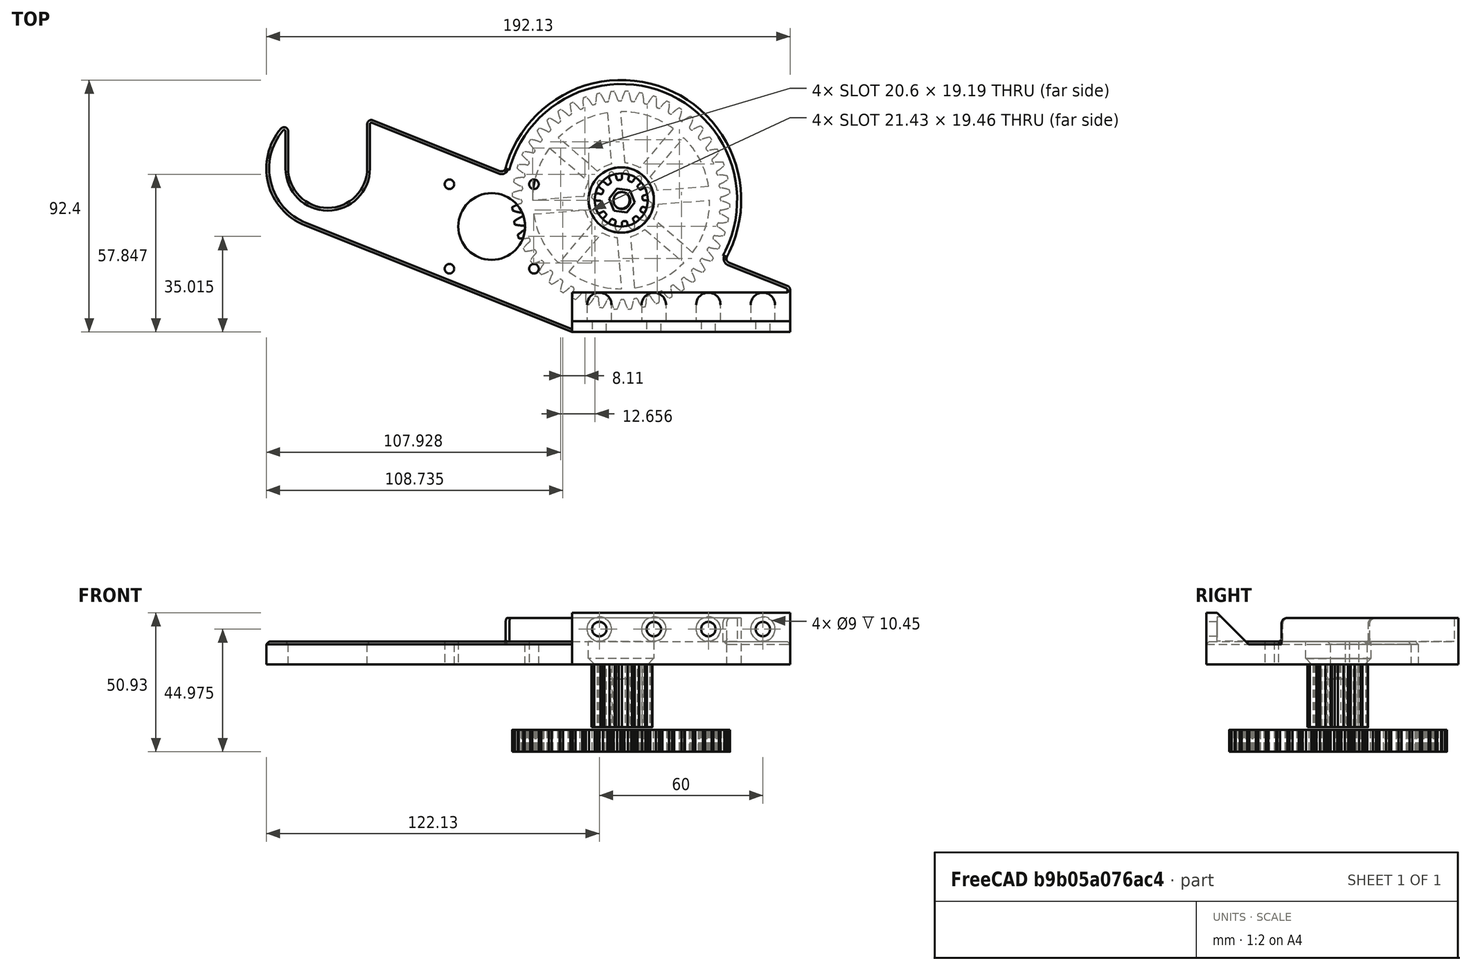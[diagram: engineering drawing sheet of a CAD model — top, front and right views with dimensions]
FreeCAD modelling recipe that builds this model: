
FCSTD DOCUMENT  (FreeCAD 0.20R29177 (Git))
Label: Spool Holder_-_Part_5B_-_48t straight
License: All rights reserved
LicenseURL: http://en.wikipedia.org/wiki/All_rights_reserved
objects: Sketcher::SketchObject×7, PartDesign::Pad×3, PartDesign::Pocket×3, PartDesign::Chamfer×3, Part::Feature×2, Mesh::Feature×2, PartDesign::Plane×2, App::Part×1, PartDesign::Fillet×1, PartDesign::Body×1
note: 32 computed .brp shape members not serialized (recipe doc carries the construction recipe); baked Part::Feature solids carry a one-line shape summary decoded from their .brp

FEATURE [Sketcher::SketchObject] Sketch002
  FullyConstrained = false
  MapMode = 5
  sketch-geometry (26):
    g0: ArcOfCircle CenterX=-129.63 CenterY=60 CenterZ=0 NormalX=0 NormalY=0 NormalZ=1 AngleXU=0 Radius=14.5 StartAngle=3.14159 EndAngle=6.28317
    g1: ArcOfCircle CenterX=-129.63 CenterY=60 CenterZ=0 NormalX=0 NormalY=0 NormalZ=1 AngleXU=0 Radius=22.5 StartAngle=2.43705 EndAngle=4.33263
    g2: LineSegment StartX=-40 StartY=0 StartZ=0 EndX=40 EndY=0 EndZ=0
    g3: LineSegment StartX=40 StartY=0 StartZ=0 EndX=40 EndY=15.5052 EndZ=0
    g4: LineSegment StartX=-40 StartY=0 StartZ=0 EndX=-137.971 EndY=39.103 EndZ=0
    g5: LineSegment StartX=-113.074 StartY=77.618 StartZ=0 EndX=-66.4027 EndY=58.9901 EndZ=0
    g6: Circle CenterX=-69.469 CenterY=38.6797 CenterZ=0 NormalX=0 NormalY=0 NormalZ=1 AngleXU=0 Radius=12.25
    g7: Circle CenterX=-21.953 CenterY=48.4 CenterZ=0 NormalX=0 NormalY=0 NormalZ=1 AngleXU=0 Radius=9.75
    g8: LineSegment StartX=-144.13 StartY=60 StartZ=0 EndX=-144.13 EndY=73.6015 EndZ=0
    g9: LineSegment StartX=-115.13 StartY=59.9997 StartZ=0 EndX=-115.13 EndY=76.2248 EndZ=0
    g10: ArcOfCircle CenterX=-145.63 CenterY=73.6015 CenterZ=0 NormalX=0 NormalY=0 NormalZ=1 AngleXU=0 Radius=1.5 StartAngle=3e-15 EndAngle=2.43705
    g11: ArcOfCircle CenterX=-113.63 CenterY=76.2248 CenterZ=0 NormalX=0 NormalY=0 NormalZ=1 AngleXU=0 Radius=1.5 StartAngle=1.19104 EndAngle=3.14159
    g12: ArcOfCircle CenterX=38.5 CenterY=15.5052 CenterZ=0 NormalX=0 NormalY=0 NormalZ=1 AngleXU=0 Radius=1.5 StartAngle=0 EndAngle=1.19104
    g13: ArcOfCircle CenterX=-21.953 CenterY=48.4 CenterZ=0 NormalX=0 NormalY=0 NormalZ=1 AngleXU=0 Radius=44 StartAngle=5.79018 EndAngle=9.15827
    g14: LineSegment StartX=17.5726 StartY=25.473 StartZ=0 EndX=39.056 EndY=16.8983 EndZ=0
    g15: ArcOfCircle CenterX=18.1287 CenterY=26.8661 CenterZ=0 NormalX=0 NormalY=0 NormalZ=1 AngleXU=0 Radius=1.5 StartAngle=2.64859 EndAngle=4.33263
    g16: ArcOfCircle CenterX=-65.8467 CenterY=60.3832 CenterZ=0 NormalX=0 NormalY=0 NormalZ=1 AngleXU=0 Radius=1.5 StartAngle=4.33263 EndAngle=6.01667
    g17: LineSegment StartX=-53.969 StartY=23.1797 StartZ=0 EndX=-53.969 EndY=54.1797 EndZ=0
    g18: LineSegment StartX=-53.969 StartY=54.1797 StartZ=0 EndX=-84.969 EndY=54.1797 EndZ=0
    g19: LineSegment StartX=-84.969 StartY=54.1797 StartZ=0 EndX=-84.969 EndY=23.1797 EndZ=0
    g20: LineSegment StartX=-84.969 StartY=23.1797 StartZ=0 EndX=-53.969 EndY=23.1797 EndZ=0
    g21: GeomPoint X=-69.469 Y=38.6797 Z=0
    g22: Circle CenterX=-84.969 CenterY=23.1797 CenterZ=0 NormalX=0 NormalY=0 NormalZ=1 AngleXU=0 Radius=1.75
    g23: Circle CenterX=-84.969 CenterY=54.1797 CenterZ=0 NormalX=0 NormalY=0 NormalZ=1 AngleXU=0 Radius=1.75
    g24: Circle CenterX=-53.969 CenterY=54.1797 CenterZ=0 NormalX=0 NormalY=0 NormalZ=1 AngleXU=0 Radius=1.75
    g25: Circle CenterX=-53.969 CenterY=23.1797 CenterZ=0 NormalX=0 NormalY=0 NormalZ=1 AngleXU=0 Radius=1.75
  constraints (64):
    c: Diameter(g0) = 29
    c: Coincident(g1,g0)
    c: Diameter(g1) = 45
    c: PointOnObject(g2,g-1)
    c: PointOnObject(g2,g-1)
    c: Vertical(g3)
    c: DistanceX(g0) = -129.63
    c: DistanceY(g-1,g0) = 60
    c: Parallel(g5,g4)
    c: Diameter(g6) = 24.5
    c: Diameter(g7) = 19.5
    c: Distance(g7,g0) = 108.3
    c: Distance(g6,g7) = 48.5
    c: DistanceY(g4,g7) = 48.4
    c: Vertical(g8)
    c: Tangent(g0,g8) = 1.5708
    c: Vertical(g9)
    c: Tangent(g1,g4) = 1.5708
    c: Tangent(g8,g10) = -1.5708
    c: Tangent(g1,g10) = -1.5708
    c: Diameter(g10) = 3
    c: Tangent(g5,g11) = 1.5708
    c: Tangent(g9,g11) = 1.5708
    c: Diameter(g11) = 3
    c: Tangent(g3,g12) = -1.5708
    c: Diameter(g12) = 3
    c: DistanceX(g2,g-1) = 40
    c: DistanceX(g2,g2) = 80
    c: Coincident(g4,g2)
    c: Distance(g6,g4) = 25
    c: Coincident(g9,g0)
    c: Distance(g2,g5) = 45
    c: Coincident(g3,g2)
    c: Tangent(g13,g15) = 1.5708
    c: Tangent(g14,g15) = -1.5708
    c: Tangent(g13,g16) = 1.5708
    c: Tangent(g5,g16) = -1.5708
    c: Equal(g12,g15)
    c: Equal(g15,g16)
    c: Diameter(g13) = 88
    c: Coincident(g7,g13)
    c: PointOnObject(g14,g5)
    c: PointOnObject(g12,g5)
    c: Tangent(g14,g12) = 1.5708
    c: Coincident(g17,g18)
    c: Coincident(g18,g19)
    c: Coincident(g19,g20)
    c: Coincident(g20,g17)
    c: Horizontal(g18)
    c: Horizontal(g20)
    c: Vertical(g17)
    c: Vertical(g19)
    c: Symmetric(g18,g17,g21)
    c: Coincident(g21,g6)
    c: DistanceX(g18,g18) = 31
    c: Equal(g18,g19)
    c: Coincident(g22,g19)
    c: Coincident(g23,g18)
    c: Coincident(g24,g17)
    c: Coincident(g25,g17)
    c: Equal(g22,g23)
    c: Equal(g23,g24)
    c: Equal(g24,g25)
    c: Diameter(g22) = 3.5
FEATURE [PartDesign::Pad] Pad
  Direction = (0,0,1)
  Length = 8.425
  Length2 = 10
  Profile = -> Sketch002
  ReferenceAxis = -> Sketch002 [N_Axis]
  Type = 0
FEATURE [Part::Feature] Part__Feature  label="PolarPattern"
  Placement = pos=(-22,48.3,-9) rot=(0,0,1;1.64934rad)
  shape: bbox 79.95 x 79.95 x 8 mm, 323 faces (baked)
FEATURE [Part::Feature] Part__Feature001  label="Cut002"
  Placement = pos=(-21.7,48.2,0) rot=(0,0,-1;0.143117rad)
  shape: bbox 22.29 x 22.29 x 23 mm, 106 faces (baked)
FEATURE [App::Part] TOP___Part_5C___DoubleGear48t
  Group = -> [Part__Feature,Part__Feature001]
  Origin = -> Origin001
  Placement = pos=(0,0,38) rot=(0,0,1;0rad)
FEATURE [Sketcher::SketchObject] Sketch
  ExternalGeometry = -> [Pad]
  FullyConstrained = false
  MapMode = 5
  Support = -> [XY_Plane]
  sketch-geometry (4):
    g0: ArcOfCircle CenterX=-21.9529 CenterY=48.4002 CenterZ=0 NormalX=0 NormalY=0 NormalZ=1 AngleXU=0 Radius=42.51 StartAngle=5.78619 EndAngle=9.16226
    g1: LineSegment StartX=-64.3996 StartY=59.9882 StartZ=0 EndX=-63.0065 EndY=59.4321 EndZ=0
    g2: LineSegment StartX=15.4142 StartY=28.1321 StartZ=0 EndX=16.8073 EndY=27.576 EndZ=0
    g3: ArcOfCircle CenterX=-21.9529 CenterY=48.4002 CenterZ=0 NormalX=0 NormalY=0 NormalZ=1 AngleXU=0 Radius=44 StartAngle=5.79018 EndAngle=9.15827
  constraints (10):
    c: Coincident(g1,g-3)
    c: Coincident(g2,g-3)
    c: Coincident(g0,g1)
    c: Coincident(g0,g2)
    c: Equal(g1,g2)
    c: Distance(g1) = 1.5
    c: Parallel(g1,g2)
    c: Coincident(g3,g0)
    c: Coincident(g3,g2)
    c: Coincident(g3,g1)
FEATURE [PartDesign::Pad] Pad001
  BaseFeature = -> Pad
  Direction = (0,0,1)
  Length = 17
  Length2 = 10
  Profile = -> Sketch
  ReferenceAxis = -> Sketch [N_Axis]
  Type = 0
FEATURE [Mesh::Feature] RECREATOR3D___Part_6A___Spool_Gear  label="RECREATOR3D - Part 6A - Spool Gear"
  Placement = pos=(-129.6,60,0) rot=(0,0,1;0.07854rad)
FEATURE [Mesh::Feature] RECREATOR3D___Part_8___Small_Gear_WIDER  label="RECREATOR3D - Part 8 - Small Gear WIDER"
  Placement = pos=(-69.3,38.6,0) rot=(0,0,1;0.106465rad)
FEATURE [Sketcher::SketchObject] Sketch003
  ExternalGeometry = -> [Pad001]
  FullyConstrained = true
  MapMode = 5
  Placement = pos=(0,0,0) rot=(0.57735,0.57735,0.57735;2.0944rad)
  Support = -> [YZ_Plane]
  sketch-geometry (4):
    g0: LineSegment StartX=0 StartY=18.925 StartZ=0 EndX=4 EndY=18.925 EndZ=0
    g1: LineSegment StartX=4 StartY=18.925 StartZ=0 EndX=14.5 EndY=8.425 EndZ=0
    g2: LineSegment StartX=0 StartY=8.425 StartZ=0 EndX=14.5 EndY=8.425 EndZ=0
    g3: LineSegment StartX=0 StartY=18.925 StartZ=0 EndX=0 EndY=8.425 EndZ=0
  constraints (11):
    c: PointOnObject(g0,g-2)
    c: Horizontal(g0)
    c: Coincident(g1,g0)
    c: PointOnObject(g1,g-3)
    c: Angle(g0,g1) = 2.35619
    c: DistanceX(g0,g0) = 4
    c: Coincident(g2,g-3)
    c: Coincident(g2,g1)
    c: Coincident(g3,g0)
    c: DistanceY(g3,g3) = 10.5
    c: Coincident(g3,g2)
FEATURE [PartDesign::Pad] Pad002
  BaseFeature = -> Pad001
  Direction = (1,-2e-16,3e-16)
  Length = 40
  Length2 = 40
  Profile = -> Sketch003
  ReferenceAxis = -> Sketch003 [N_Axis]
  Type = 4
FEATURE [Sketcher::SketchObject] Sketch004
  ExternalGeometry = -> [Pad002]
  FullyConstrained = false
  MapMode = 5
  Placement = pos=(0,0,0) rot=(1,0,0;1.5708rad)
  Support = -> [XZ_Plane]
  sketch-geometry (7):
    g0: Circle CenterX=30 CenterY=12.975 CenterZ=0 NormalX=0 NormalY=0 NormalZ=1 AngleXU=0 Radius=2.65
    g1: Circle CenterX=10 CenterY=12.975 CenterZ=0 NormalX=0 NormalY=0 NormalZ=1 AngleXU=0 Radius=2.65
    g2: LineSegment StartX=30 StartY=12.975 StartZ=0 EndX=10 EndY=12.975 EndZ=0
    g3: Circle CenterX=-10 CenterY=12.975 CenterZ=0 NormalX=0 NormalY=0 NormalZ=1 AngleXU=0 Radius=2.65
    g4: LineSegment StartX=10 StartY=12.975 StartZ=0 EndX=-10 EndY=12.975 EndZ=0
    g5: Circle CenterX=-30 CenterY=12.975 CenterZ=0 NormalX=0 NormalY=0 NormalZ=1 AngleXU=0 Radius=2.65
    g6: LineSegment StartX=-10 StartY=12.975 StartZ=0 EndX=-30 EndY=12.975 EndZ=0
  constraints (16):
    c: Diameter(g0) = 5.3
    c: Diameter(g1) = 5.3
    c: Coincident(g0,g2)
    c: Coincident(g1,g2)
    c: Distance(g2) = 20
    c: Angle(g2) = 3.14159
    c: Diameter(g3) = 5.3
    c: Coincident(g1,g4)
    c: Coincident(g3,g4)
    c: Equal(g2,g4)
    c: Parallel(g4,g2)
    c: Diameter(g5) = 5.3
    c: Coincident(g3,g6)
    c: Coincident(g5,g6)
    c: Equal(g2,g6)
    c: Parallel(g6,g2)
FEATURE [PartDesign::Pocket] Pocket
  BaseFeature = -> Pad002
  Direction = (0,1,2e-16)
  Length = 18
  Length2 = 5
  Profile = -> Sketch004
  ReferenceAxis = -> Sketch004 [N_Axis]
  Type = 0
FEATURE [PartDesign::Plane] DatumPlane  label="CounterBorePlane"
  AttachmentOffset = pos=(0,0,-4) rot=(0,0,1;0rad)
  Length = 211.732
  MapMode = 5
  Placement = pos=(9e-16,4,-9e-16) rot=(1,0,0;1.5708rad)
  ResizeMode = 0
  Support = -> [Pocket]
  Width = 69.6025
FEATURE [Sketcher::SketchObject] Sketch005
  ExternalGeometry = -> [Pocket]
  FullyConstrained = false
  MapMode = 5
  Placement = pos=(9e-16,4,-9e-16) rot=(1,0,0;1.5708rad)
  Support = -> [DatumPlane]
  sketch-geometry (4):
    g0: Circle CenterX=-30 CenterY=12.975 CenterZ=0 NormalX=0 NormalY=0 NormalZ=1 AngleXU=0 Radius=4.5
    g1: Circle CenterX=-10 CenterY=12.975 CenterZ=0 NormalX=0 NormalY=0 NormalZ=1 AngleXU=0 Radius=4.5
    g2: Circle CenterX=10 CenterY=12.975 CenterZ=0 NormalX=0 NormalY=0 NormalZ=1 AngleXU=0 Radius=4.5
    g3: Circle CenterX=30 CenterY=12.975 CenterZ=0 NormalX=0 NormalY=0 NormalZ=1 AngleXU=0 Radius=4.5
  constraints (7):
    c: Coincident(g1,g-4)
    c: Coincident(g2,g-5)
    c: Coincident(g3,g-6)
    c: Diameter(g3) = 9
    c: Equal(g3,g2)
    c: Equal(g2,g1)
    c: Equal(g1,g0)
FEATURE [PartDesign::Pocket] Pocket001
  BaseFeature = -> Pocket
  Direction = (2e-16,1,-2e-16)
  Length = 12
  Length2 = 5
  Profile = -> Sketch005
  ReferenceAxis = -> Sketch005 [N_Axis]
  Type = 0
FEATURE [Sketcher::SketchObject] Sketch006
  FullyConstrained = true
  MapMode = 5
  Support = -> [XY_Plane]
FEATURE [PartDesign::Plane] DatumPlane001
  Length = 222.164
  MapMode = 5
  Placement = pos=(0,0,8.425) rot=(0,0,1;0rad)
  ResizeMode = 0
  Support = -> [Pad001]
  Width = 147.415
FEATURE [Sketcher::SketchObject] Sketch007
  ExternalGeometry = -> [Pad001]
  FullyConstrained = true
  MapMode = 5
  Placement = pos=(0,0,8.425) rot=(0,0,1;0rad)
  Support = -> [DatumPlane001]
  sketch-geometry (1):
    g0: Circle CenterX=-21.953 CenterY=48.4 CenterZ=0 NormalX=0 NormalY=0 NormalZ=1 AngleXU=0 Radius=12
  constraints (2):
    c: Coincident(g0,g-3)
    c: Diameter(g0) = 24
FEATURE [PartDesign::Pocket] Pocket002
  BaseFeature = -> Pocket001
  Direction = (0,0,-1)
  Length = 6.2
  Length2 = 5
  Profile = -> Sketch007
  ReferenceAxis = -> Sketch007 [N_Axis]
  Type = 0
FEATURE [PartDesign::Chamfer] Chamfer
  Angle = 45
  Base = -> Pocket002 [Edge72]
  BaseFeature = -> Pocket002
  ChamferType = 0
  FlipDirection = false
  Size = 2.2
  Size2 = 1
  SupportTransform = false
  UseAllEdges = false
FEATURE [PartDesign::Fillet] Fillet
  Base = -> Chamfer [Edge93,Edge101]
  BaseFeature = -> Chamfer
  Radius = 2
  SupportTransform = false
  UseAllEdges = false
FEATURE [PartDesign::Chamfer] Chamfer001
  Angle = 45
  Base = -> Fillet [Edge29,Edge27,Edge28]
  BaseFeature = -> Fillet
  ChamferType = 0
  FlipDirection = false
  Size = 1
  Size2 = 1
  SupportTransform = false
  UseAllEdges = false
FEATURE [PartDesign::Chamfer] Chamfer002
  Angle = 45
  Base = -> Chamfer001 [Edge64]
  BaseFeature = -> Chamfer001
  ChamferType = 0
  FlipDirection = false
  Size = 1
  Size2 = 1
  SupportTransform = false
  UseAllEdges = false
FEATURE [PartDesign::Body] Body
  Group = -> [Sketch002,Pad,Sketch,Pad001,Sketch003,Pad002,Sketch004,Pocket,DatumPlane,Sketch005,Pocket001,Sketch006,DatumPlane001,Sketch007,Pocket002,Chamfer,Fillet,Chamfer001,Chamfer002]
  Origin = -> Origin
  Tip = -> Chamfer002
